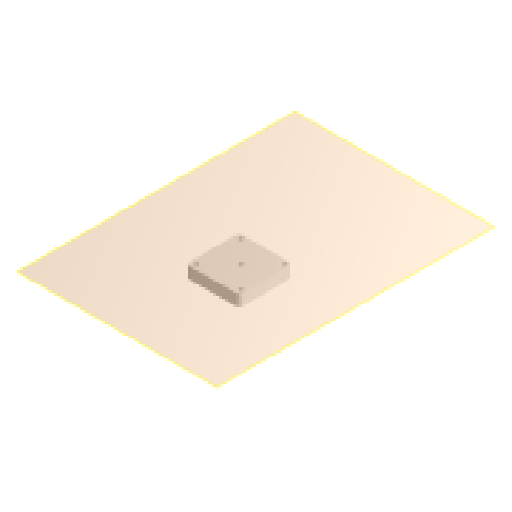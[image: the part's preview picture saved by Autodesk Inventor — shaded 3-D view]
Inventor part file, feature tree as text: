
AUTODESK INVENTOR PART (.ipt)
format: ipt  version: 2024.1 (Build 281209000, 209)  size: 121,856 bytes
history: native  units: mm
features: other x4, reference x2, plane x1, extrude x1, sketch x1
ambient origin geometry x8: Origin, YZ Plane, XZ Plane, XY Plane, X Axis, Y Axis, Z Axis, Center Point
bodies: Volumenkörper1 (feature_tree)
feature tree (9):
  plane  "Arbeitsebene1"
  extrude  "Extrusion1"  Depth=6.0mm
  sketch  "Skizze1"  dims[d0=3.0mm d1=2.8mm d2=2.8mm d3=2.8mm d4=2.8mm d5=6.0mm d6=0.0mm]
  reference  "Referenz1"
  reference  "Referenz2"
  other  "Assembly_Planktoscope_Uc2version_wormdrive_V3.iam"
  other  "00_Micro_Stepper_15mm_Gearbox_NEMA17Adapter:1"
  other  "00_Micro_Stepper_15mm_Gearbox:1"
  other  "60_Planktoscope_Base_half1_MIR:1"
